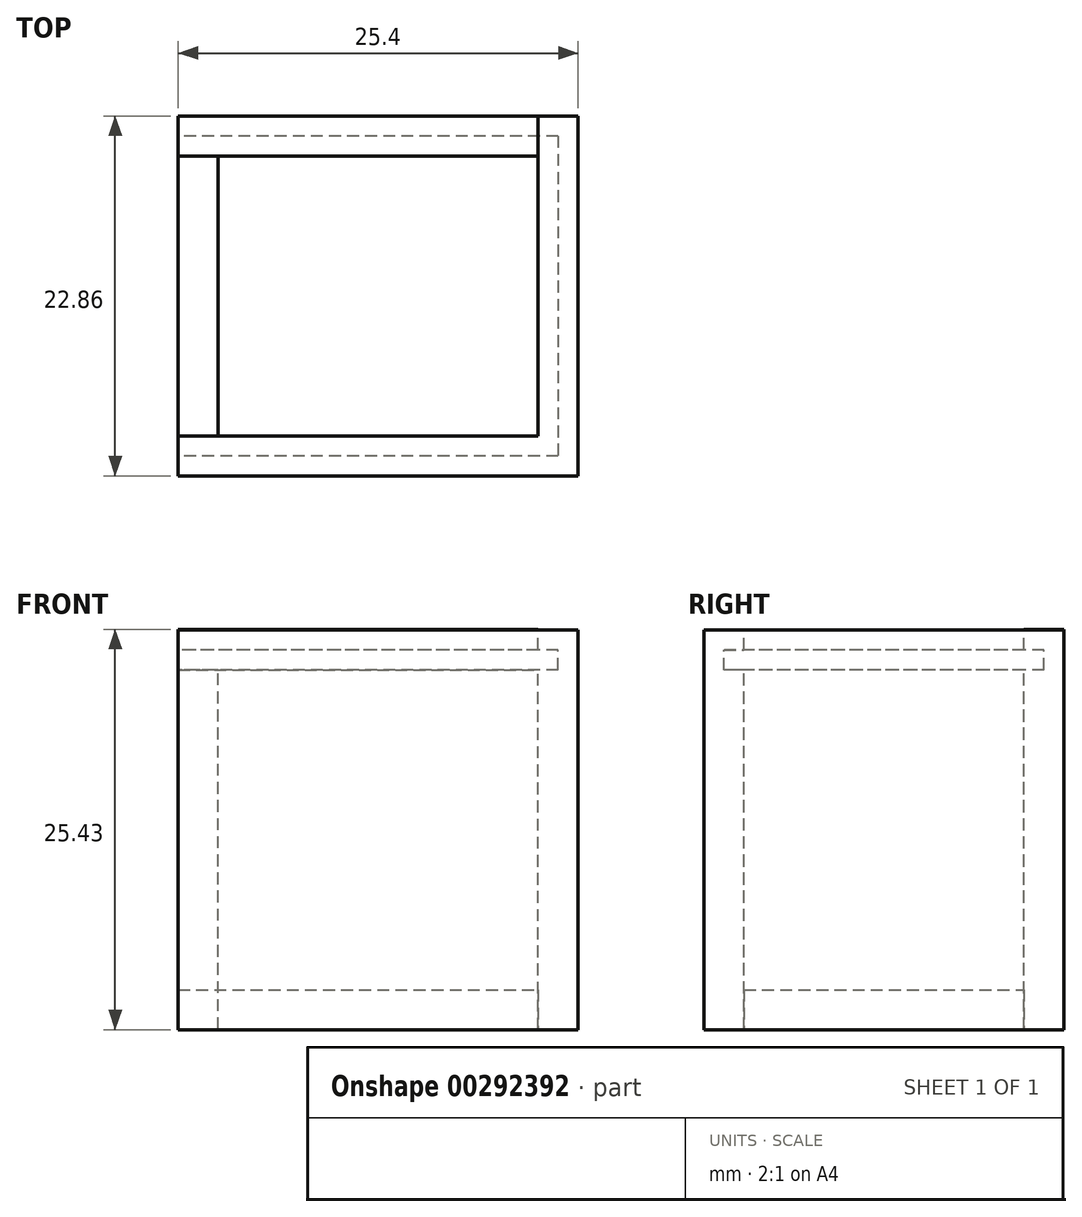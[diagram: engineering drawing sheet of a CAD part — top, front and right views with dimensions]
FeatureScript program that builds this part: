
annotation { "Feature Type Name" : "Feature", "Feature Type Description" : "" }
export const myFeature = defineFeature(function(context is Context, id is Id, definition is map)
    precondition{}
    {
        {
            var Q0;
            Q0=qCreatedBy(makeId("Front.planeOp"),FACE);
            var sketch = newSketch(context, id + "F0", { "sketchPlane" : qUnion([Q0])});
            skLineSegment(sketch, "E0.bottom", {"start": v(0, 0) * mm, "end": v(25.4, 0) * mm});
            skLineSegment(sketch, "E0.top", {"start": v(0, 25.4) * mm, "end": v(25.4, 25.4) * mm});
            skLineSegment(sketch, "E0.left", {"start": v(0, 0) * mm, "end": v(0, 25.4) * mm});
            skLineSegment(sketch, "E0.right", {"start": v(25.4, 0) * mm, "end": v(25.4, 25.4) * mm});
            skSolve(sketch);
        }
        {
            var Q0;
            Q0=makeQuery(id+"F0.imprint","IMPRINT",FACE,{"disambiguationData":[TD([[makeQuery(id+"F0.imprint","IMPRINT",EDGE,{"derivedFrom":sQuery(id+"F0.wireOp",EDGE,"E0.bottom")}),1.0]])]});
            extrude(context, id + "F1", {"entities" : qUnion([Q0]), "depth" : 2.54 * mm});
        }
        {
            var Q0;
            Q0=makeQuery(id+"F1.opExtrude","SWEPT_FACE",FACE,{"disambiguationData":[OSD([sQuery(id+"F0.wireOp",EDGE,"E0.right")])]});
            var sketch = newSketch(context, id + "F2", { "sketchPlane" : qUnion([Q0])});
            skLineSegment(sketch, "E1.bottom", {"start": v(0, 0) * mm, "end": v(20.32, 0) * mm});
            skLineSegment(sketch, "E1.top", {"start": v(0, 25.4) * mm, "end": v(20.32, 25.4) * mm});
            skLineSegment(sketch, "E1.left", {"start": v(0, 0) * mm, "end": v(0, 25.4) * mm});
            skLineSegment(sketch, "E1.right", {"start": v(20.32, 0) * mm, "end": v(20.32, 25.4) * mm});
            skSolve(sketch);
        }
        {
            var Q0;
            Q0=makeQuery(id+"F2.imprint","IMPRINT",FACE,{"disambiguationData":[TD([[makeQuery(id+"F2.imprint","IMPRINT",EDGE,{"derivedFrom":sQuery(id+"F2.wireOp",EDGE,"E1.bottom")}),1.0]])]});
            extrude(context, id + "F3", {"entities" : qUnion([Q0]), "operationType" : NewBodyOperationType.ADD, "oppositeDirection" : true, "depth" : 2.54 * mm});
        }
        {
            var Q0;
            Q0=makeQuery(id+"F3.opExtrude","SWEPT_FACE",FACE,{"disambiguationData":[OSD([sQuery(id+"F2.wireOp",EDGE,"E1.right")])]});
            var sketch = newSketch(context, id + "F4", { "sketchPlane" : qUnion([Q0])});
            skLineSegment(sketch, "E2.bottom", {"start": v(-22.86, 0) * mm, "end": v(0, 0) * mm});
            skLineSegment(sketch, "E2.top", {"start": v(-22.86, 25.43) * mm, "end": v(0, 25.43) * mm});
            skLineSegment(sketch, "E2.left", {"start": v(-22.86, 0) * mm, "end": v(-22.86, 25.43) * mm});
            skLineSegment(sketch, "E2.right", {"start": v(0, 0) * mm, "end": v(0, 25.43) * mm});
            skSolve(sketch);
        }
        {
            var Q0;
            {var subQ4=sQuery(id+"F4.wireOp",EDGE,"E2.bottom");Q0=makeQuery(id+"F4.imprint","IMPRINT",FACE,{"disambiguationData":[TD([[makeQuery(id+"F4.imprint","IMPRINT",EDGE,{"derivedFrom":subQ4}),1.0]])]});}
            extrude(context, id + "F5", {"entities" : qUnion([Q0]), "operationType" : NewBodyOperationType.ADD, "oppositeDirection" : true, "depth" : 2.54 * mm});
        }
        {
            var Q0;
            Q0=makeQuery(id+"F5.opExtrude","SWEPT_FACE",FACE,{"disambiguationData":[OSD([sQuery(id+"F4.wireOp",EDGE,"E2.top")])]});
            var sketch = newSketch(context, id + "F6", { "sketchPlane" : qUnion([Q0])});
            skLineSegment(sketch, "E3.bottom", {"start": v(0, 17.78) * mm, "end": v(2.54, 17.78) * mm});
            skLineSegment(sketch, "E3.top", {"start": v(0, 0) * mm, "end": v(2.54, 0) * mm});
            skLineSegment(sketch, "E3.left", {"start": v(0, 17.78) * mm, "end": v(0, 0) * mm});
            skLineSegment(sketch, "E3.right", {"start": v(2.54, 17.78) * mm, "end": v(2.54, 0) * mm});
            skSolve(sketch);
        }
        {
            var Q0;
            Q0=makeQuery(id+"F6.imprint","IMPRINT",FACE,{"disambiguationData":[TD([[makeQuery(id+"F6.imprint","IMPRINT",EDGE,{"derivedFrom":sQuery(id+"F6.wireOp",EDGE,"E3.bottom")}),1.0]])]});
            extrude(context, id + "F7", {"entities" : qUnion([Q0]), "oppositeDirection" : true, "depth" : 25.4 * mm});
        }
        {
            var Q0;
            Q0=qCreatedBy(makeId("Top.planeOp"),FACE);
            var sketch = newSketch(context, id + "F8", { "sketchPlane" : qUnion([Q0])});
            skLineSegment(sketch, "E4.bottom", {"start": v(0, 0) * mm, "end": v(22.86, 0) * mm});
            skLineSegment(sketch, "E4.top", {"start": v(0, 17.78) * mm, "end": v(22.86, 17.78) * mm});
            skLineSegment(sketch, "E4.left", {"start": v(0, 0) * mm, "end": v(0, 17.78) * mm});
            skLineSegment(sketch, "E4.right", {"start": v(22.86, 0) * mm, "end": v(22.86, 17.78) * mm});
            skSolve(sketch);
        }
        {
            var Q0;
            Q0=makeQuery(id+"F8.imprint","IMPRINT",FACE,{"disambiguationData":[TD([[makeQuery(id+"F8.imprint","IMPRINT",EDGE,{"derivedFrom":sQuery(id+"F8.wireOp",EDGE,"E4.bottom")}),1.0]])]});
            extrude(context, id + "F9", {"entities" : qUnion([Q0]), "depth" : 2.54 * mm});
        }
        {
            var Q0;
            Q0=makeQuery(id+"F7.opExtrude","SWEPT_FACE",FACE,{"disambiguationData":[OSD([sQuery(id+"F6.wireOp",EDGE,"E3.left")])]});
            var sketch = newSketch(context, id + "F10", { "sketchPlane" : qUnion([Q0])});
            skLineSegment(sketch, "E5", {"start": v(0, 22.86) * mm, "end": v(1.27, 22.86) * mm});
            skLineSegment(sketch, "E6", {"start": v(1.27, 22.86) * mm, "end": v(1.27, 24.13) * mm});
            skLineSegment(sketch, "E7", {"start": v(0, 22.86) * mm, "end": v(-19.05, 22.86) * mm});
            skLineSegment(sketch, "E8", {"start": v(-19.05, 22.86) * mm, "end": v(-19.05, 24.13) * mm});
            skLineSegment(sketch, "E9", {"start": v(-19.05, 24.13) * mm, "end": v(-17.78, 24.13) * mm});
            skLineSegment(sketch, "E10", {"start": v(1.27, 24.13) * mm, "end": v(0, 24.13) * mm});
            skLineSegment(sketch, "E11", {"start": v(0, 24.13) * mm, "end": v(0, 25.43) * mm});
            skLineSegment(sketch, "E12", {"start": v(0, 25.43) * mm, "end": v(-17.78, 25.43) * mm});
            skLineSegment(sketch, "E13", {"start": v(-17.78, 25.43) * mm, "end": v(-17.78, 24.13) * mm});
            skSolve(sketch);
        }
        {
            var Q0;
            {var subQ0=sQuery(id+"F10.wireOp",EDGE,"E5");Q0=makeQuery(id+"F10.imprint","IMPRINT",FACE,{"disambiguationData":[TD([[makeQuery(id+"F10.imprint","IMPRINT",EDGE,{"derivedFrom":subQ0}),1.0]])]});}
            var Q1;
            {var subQ1=sQuery(id+"F10.wireOp",EDGE,"E11");Q1=makeQuery(id+"F10.imprint","IMPRINT",FACE,{"disambiguationData":[TD([[makeQuery(id+"F10.imprint","IMPRINT",EDGE,{"derivedFrom":subQ1}),1.0]])]});}
            var Q2;
            {var subQ0=sQuery(id+"F10.wireOp",EDGE,"E8");Q2=makeQuery(id+"F10.imprint","IMPRINT",FACE,{"disambiguationData":[TD([[makeQuery(id+"F10.imprint","IMPRINT",EDGE,{"derivedFrom":subQ0}),-1.0]])]});}
            extrude(context, id + "F11", {"entities" : qUnion([Q0, Q1, Q2]), "operationType" : NewBodyOperationType.REMOVE, "oppositeDirection" : true, "depth" : 22.86 * mm});
        }
        {
            var Q0;
            Q0=makeQuery(id+"F11.boolean.opBoolean","MERGE",FACE,{"derivedFrom":[makeQuery(id+"F3.opExtrude","CAP_FACE",FACE,{"disambiguationData":[OSD([sQuery(id+"F2.wireOp",EDGE,"E1.bottom"),sQuery(id+"F2.wireOp",EDGE,"E1.top"),sQuery(id+"F2.wireOp",EDGE,"E1.left"),sQuery(id+"F2.wireOp",EDGE,"E1.right")])],"isStart":false}),makeQuery(id+"F11.opExtrude","CAP_FACE",FACE,{"disambiguationData":[OSD([sQuery(id+"F10.wireOp",EDGE,"E5"),sQuery(id+"F10.wireOp",EDGE,"E6"),sQuery(id+"F10.wireOp",EDGE,"E7"),sQuery(id+"F10.wireOp",EDGE,"E8"),sQuery(id+"F10.wireOp",EDGE,"E9"),sQuery(id+"F10.wireOp",EDGE,"E10"),sQuery(id+"F10.wireOp",EDGE,"E11"),sQuery(id+"F10.wireOp",EDGE,"E12"),sQuery(id+"F10.wireOp",EDGE,"E13")])],"isStart":false})]});
            var sketch = newSketch(context, id + "F12", { "sketchPlane" : qUnion([Q0])});
            skLineSegment(sketch, "E14.bottom", {"start": v(-19.05, 24.13) * mm, "end": v(1.27, 24.13) * mm});
            skLineSegment(sketch, "E14.top", {"start": v(-19.05, 22.86) * mm, "end": v(1.27, 22.86) * mm});
            skLineSegment(sketch, "E14.left", {"start": v(-19.05, 24.13) * mm, "end": v(-19.05, 22.86) * mm});
            skLineSegment(sketch, "E14.right", {"start": v(1.27, 24.13) * mm, "end": v(1.27, 22.86) * mm});
            skSolve(sketch);
        }
        {
            var Q0;
            {var subQ0=sQuery(id+"F12.wireOp",EDGE,"E14.left");Q0=makeQuery(id+"F12.imprint","IMPRINT",FACE,{"disambiguationData":[TD([[makeQuery(id+"F12.imprint","IMPRINT",EDGE,{"derivedFrom":subQ0}),-1.0]])]});}
            extrude(context, id + "F13", {"entities" : qUnion([Q0]), "operationType" : NewBodyOperationType.REMOVE, "oppositeDirection" : true, "depth" : 1.27 * mm});
        }
    });
